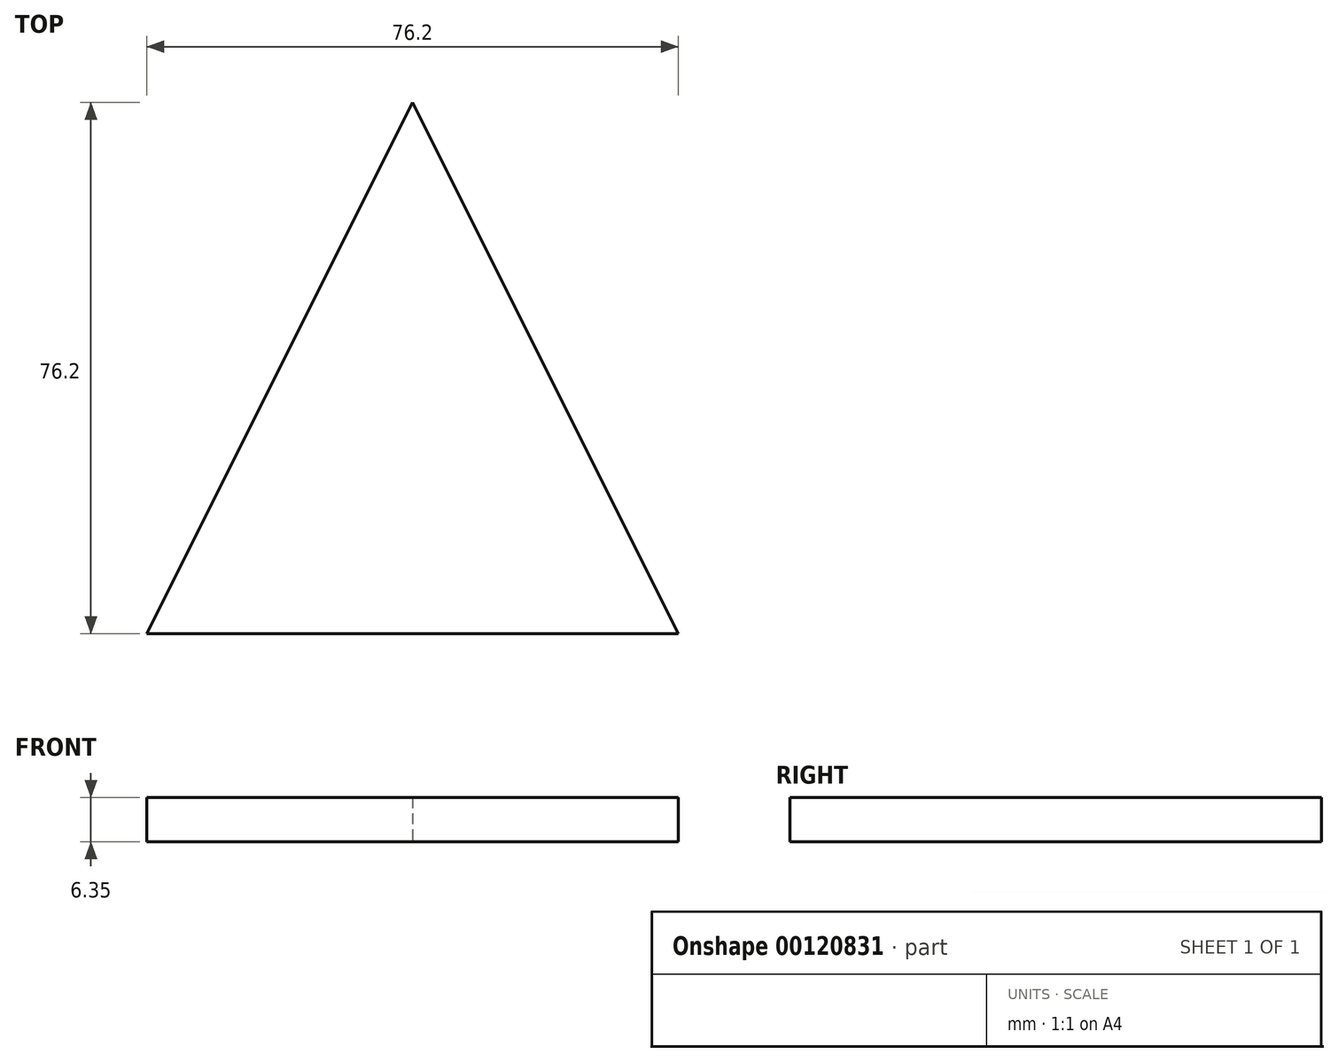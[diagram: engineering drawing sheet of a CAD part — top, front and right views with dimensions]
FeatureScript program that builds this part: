
annotation { "Feature Type Name" : "Feature", "Feature Type Description" : "" }
export const myFeature = defineFeature(function(context is Context, id is Id, definition is map)
    precondition{}
    {
        {
            var Q0;
            Q0=qCreatedBy(makeId("Top.planeOp"),FACE);
            var sketch = newSketch(context, id + "F0", { "sketchPlane" : qUnion([Q0])});
            skLineSegment(sketch, "E0", {"start": v(-38.1, 0) * mm, "end": v(38.1, 0) * mm});
            skLineSegment(sketch, "E1", {"start": v(0, 0) * mm, "end": v(0, 76.2) * mm, "construction": true});
            skLineSegment(sketch, "E2", {"start": v(-38.1, 0) * mm, "end": v(0, 76.2) * mm});
            skLineSegment(sketch, "E3", {"start": v(0, 76.2) * mm, "end": v(38.1, 0) * mm});
            skSolve(sketch);
        }
        {
            var Q0;
            Q0 = qSketchRegion(id + "F0", true);
            extrude(context, id + "F1", {"entities" : qUnion([Q0]), "depth" : 6.35 * mm});
        }
    });
